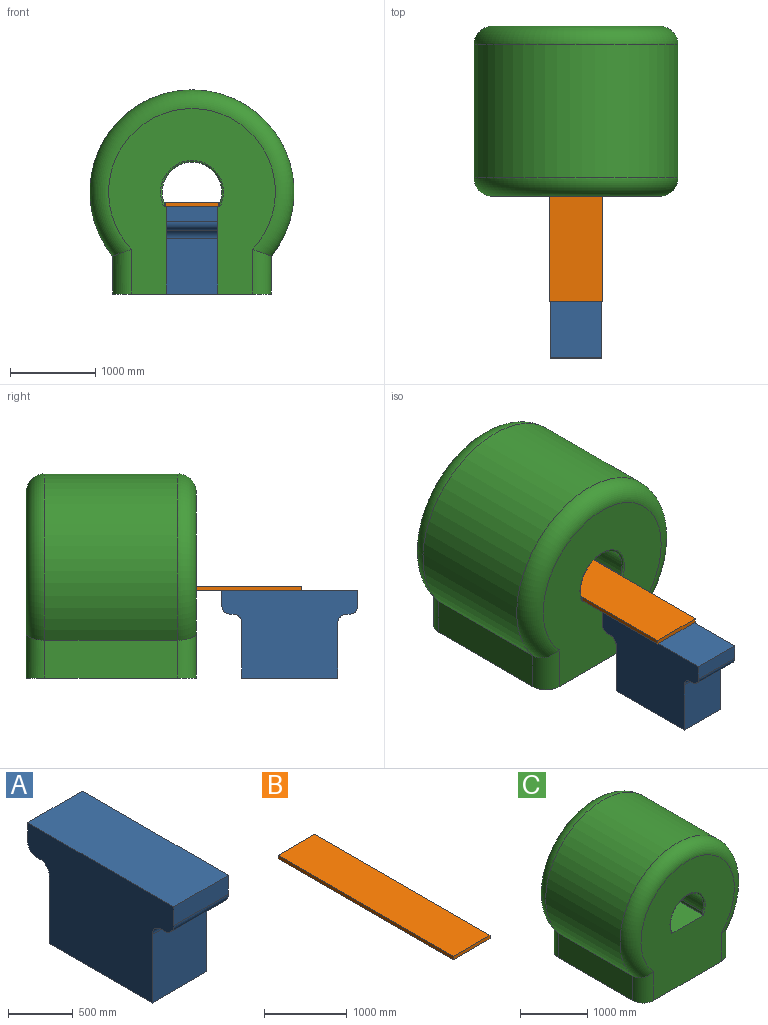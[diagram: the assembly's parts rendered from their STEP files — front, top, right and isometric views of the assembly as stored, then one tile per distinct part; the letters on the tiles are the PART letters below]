
ASSEMBLY  parts=3 mates=2
PART A: 14 faces, bbox 600x1600x1030 mm
  f0: plane 1600x600mm, normal (0,0,1), area 960000mm2, adj f1,f7,f8,f9
  f1: plane 600x180mm, normal (0,-1,0), area 108000mm2, adj f0,f8,f9,f10
  f2: plane 600x34.74mm, normal (0,0,-1), area 20843.7mm2, adj f8,f9,f10,f11
  f3: plane 650x600mm, normal (0,-1,0), area 390000mm2, adj f4,f8,f9,f11
  f4: plane 1130.52x600mm, normal (0,0,-1), area 678312.5mm2, adj f3,f5,f8,f9
  f5: plane 650x600mm, normal (0,1,0), area 390000mm2, adj f4,f8,f9,f12
  f6: plane 600x34.74mm, normal (0,0,-1), area 20843.7mm2, adj f8,f9,f12,f13
  f7: plane 600x180mm, normal (0,1,0), area 108000mm2, adj f0,f8,f9,f13
  f8: plane 1600x1030mm, normal (1,0,0), area 1295890.7mm2, adj f0,f1,f2,f3,f4,f5,f6,f7
  f9: plane 1600x1030mm, normal (-1,0,0), area 1295890.7mm2, adj f0,f1,f2,f3,f4,f5,f6,f7
  f10: cylinder r=100mm len=600mm, axis (-1,0,0), area 94247.8mm2, adj f1,f2,f8,f9
  f11: cylinder r=100mm len=600mm, axis (1,0,0), area 94247.8mm2, adj f2,f3,f8,f9
  f12: cylinder r=100mm len=600mm, axis (1,0,0), area 94247.8mm2, adj f5,f6,f8,f9
  f13: cylinder r=100mm len=600mm, axis (-1,0,0), area 94247.8mm2, adj f6,f7,f8,f9
PART B: 6 faces, bbox 630x3000x50 mm
  f0: plane 3000x630mm, normal (0,0,-1), area 1890000mm2, adj f1,f3,f4,f5
  f1: plane 630x50mm, normal (0,1,0), area 31500mm2, adj f0,f2,f4,f5
  f2: plane 3000x630mm, normal (0,0,1), area 1890000mm2, adj f1,f3,f4,f5
  f3: plane 630x50mm, normal (0,-1,0), area 31500mm2, adj f0,f2,f4,f5
  f4: plane 3000x50mm, normal (1,0,0), area 150000mm2, adj f0,f1,f2,f3
  f5: plane 3000x50mm, normal (-1,0,0), area 150000mm2, adj f0,f1,f2,f3
PART C: 18 faces, bbox 2597.7x2000x2498.9 mm
  f0: cylinder r=350mm len=1960mm, axis (0,1,0), area 2635273.2mm2, adj f13,f15,f16,f17
  f1: plane 2180x1960mm, normal (0,1,0), area 3129815.5mm2, adj f3,f7,f8,f9,f13,f14,f15,f16
  f2: plane 1560x444.81mm, normal (-1,0,0), area 693906.1mm2, adj f3,f5,f8,f11
  f3: plane 2000x1865.14mm, normal (0,0,-1), area 3688741mm2, adj f1,f2,f4,f6,f7,f8,f10,f11
  f4: plane 1560x444.81mm, normal (1,0,0), area 693906.1mm2, adj f3,f5,f7,f10
  f5: cylinder r=1200mm len=2400mm, axis (0,1,0), area 8429537.1mm2, adj f2,f4,f9,f12
  f6: plane 2180x1960mm, normal (0,-1,0), area 3129815.5mm2, adj f3,f10,f11,f12,f13,f14,f15,f17
  f7: cylinder r=220mm len=527.21mm, axis (0,0,1), area 163840mm2, adj f1,f3,f4,f9
  f8: cylinder r=220mm len=527.21mm, axis (0,0,-1), area 163840mm2, adj f1,f2,f3,f9
  f9: torus R=980mm, axis (0,-1,0), area 1762016.2mm2, adj f1,f5,f7,f8
  f10: cylinder r=220mm len=527.21mm, axis (0,0,-1), area 163840mm2, adj f3,f4,f6,f12
  f11: cylinder r=220mm len=527.21mm, axis (0,0,1), area 163840mm2, adj f2,f3,f6,f12
  f12: torus R=980mm, axis (0,-1,0), area 1762016.2mm2, adj f5,f6,f10,f11
  f13: plane 2000x50mm, normal (-1,0,0), area 99537.5mm2, adj f0,f1,f6,f14,f16,f17
  f14: plane 2000x657.57mm, normal (0,0,1), area 1315142.6mm2, adj f1,f6,f13,f15
  f15: plane 2000x50mm, normal (1,0,0), area 99537.5mm2, adj f0,f1,f6,f14,f16,f17
  f16: torus R=370mm, axis (0,-1,0), area 44242.8mm2, adj f0,f1,f13,f15
  f17: torus R=370mm, axis (0,-1,0), area 44243.3mm2, adj f0,f6,f13,f15
PLACE A t=(-916.32,-3448.73,-1489.35)mm
PLACE B t=(-931.32,218.56,-459.35)mm
PLACE C t=(-616.32,451.27,-289.35)mm fixed
MATE fastened C.f3 <-> A.f4  axis (0,0,-1) through (-616.32,-548.73,-1489.35)mm
MATE slider A.f1 <-> B.f3  axis (0,-1,0) through (-616.32,-3448.73,-459.35)mm
